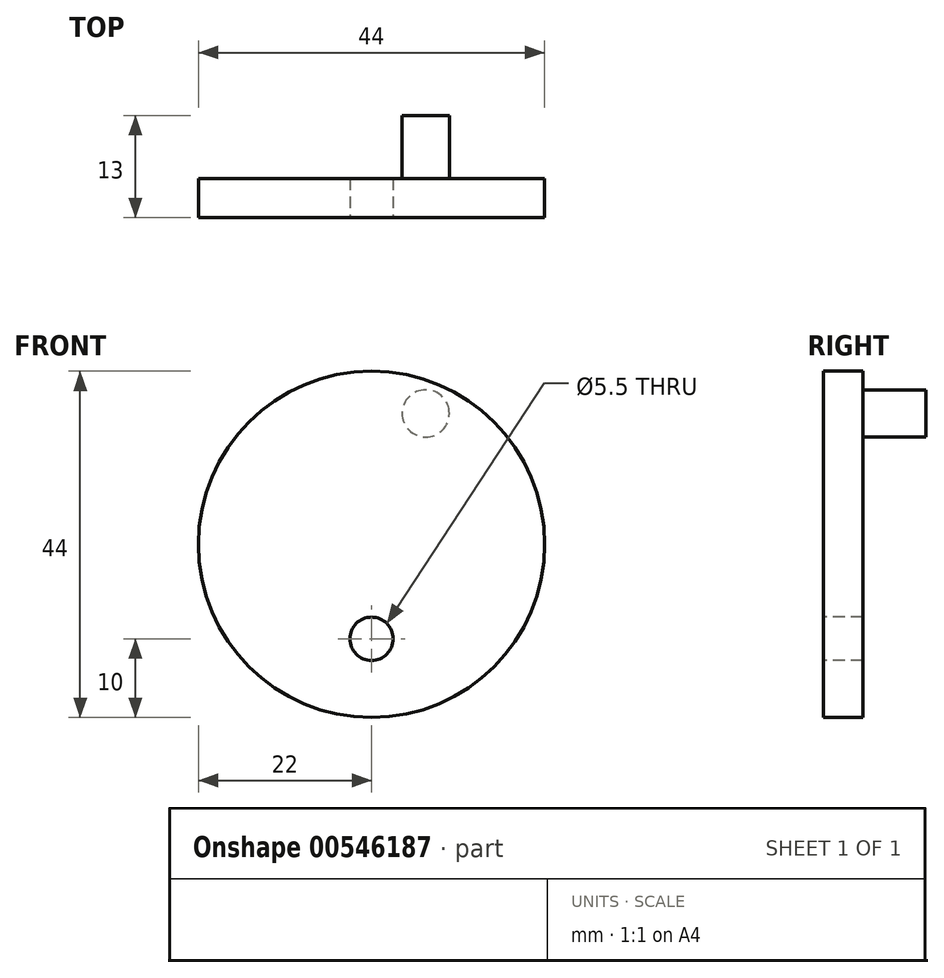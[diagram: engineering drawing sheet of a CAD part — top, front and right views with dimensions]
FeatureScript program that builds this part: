
annotation { "Feature Type Name" : "Feature", "Feature Type Description" : "" }
export const myFeature = defineFeature(function(context is Context, id is Id, definition is map)
    precondition{}
    {
        {
            var Q0;
            Q0=qCreatedBy(makeId("Front.planeOp"),FACE);
            var sketch = newSketch(context, id + "F0", { "sketchPlane" : qUnion([Q0])});
            skCircle(sketch, "E0", {"center": v(0, 0) * mm, "radius": 22 * mm});
            skSolve(sketch);
        }
        {
            var Q0;
            Q0=qSketchRegion(id+"F0",true);
            extrude(context, id + "F1", {"entities" : qUnion([Q0]), "depth" : 5 * mm, "offsetDistance" : 25 * mm});
        }
        {
            var Q0;
            Q0=makeQuery(id+"F1.opExtrude","CAP_FACE",FACE,{"disambiguationData":[OSD([sQuery(id+"F0.wireOp",EDGE,"E0")])],"isStart":false});
            var sketch = newSketch(context, id + "F2", { "sketchPlane" : qUnion([Q0])});
            skLineSegment(sketch, "E1", {"start": v(0, 0) * mm, "end": v(0, -12) * mm});
            skCircle(sketch, "E2", {"center": v(0, -12) * mm, "radius": 2.75 * mm});
            skSolve(sketch);
        }
        {
            var Q0;
            Q0=makeQuery(id+"F2.imprint","IMPRINT",FACE,{"disambiguationData":[TD([[makeQuery(id+"F2.imprint","IMPRINT",EDGE,{"derivedFrom":sQuery(id+"F2.wireOp",EDGE,"tPdcvkMc-Bunr-VTIq-aCWn-UR4HdvMpEIR7")}),1.0]])]});
            var Q1;
            Q1=makeQuery(id+"F2.imprint","IMPRINT",FACE,{"disambiguationData":[TD([[makeQuery(id+"F2.imprint","IMPRINT",EDGE,{"derivedFrom":sQuery(id+"F2.wireOp",EDGE,"E2")}),1.0]])]});
            extrude(context, id + "F3", {"entities" : qUnion([Q0, Q1]), "operationType" : NewBodyOperationType.REMOVE, "oppositeDirection" : true, "depth" : 25 * mm, "offsetDistance" : 25 * mm});
        }
        {
            var Q0;
            Q0=makeQuery(id+"F1.opExtrude","CAP_FACE",FACE,{"disambiguationData":[OSD([sQuery(id+"F0.wireOp",EDGE,"E0")])],"isStart":true});
            var sketch = newSketch(context, id + "F4", { "sketchPlane" : qUnion([Q0])});
            skCircle(sketch, "E3", {"center": v(-6.89, 16.63) * mm, "radius": 3 * mm});
            skLineSegment(sketch, "E4", {"start": v(0, 0) * mm, "end": v(-6.89, 16.63) * mm});
            skSolve(sketch);
        }
        {
            var Q0;
            Q0=qSketchRegion(id+"F4",true);
            extrude(context, id + "F5", {"entities" : qUnion([Q0]), "operationType" : NewBodyOperationType.ADD, "depth" : 8 * mm, "offsetDistance" : 25 * mm});
        }
    });
